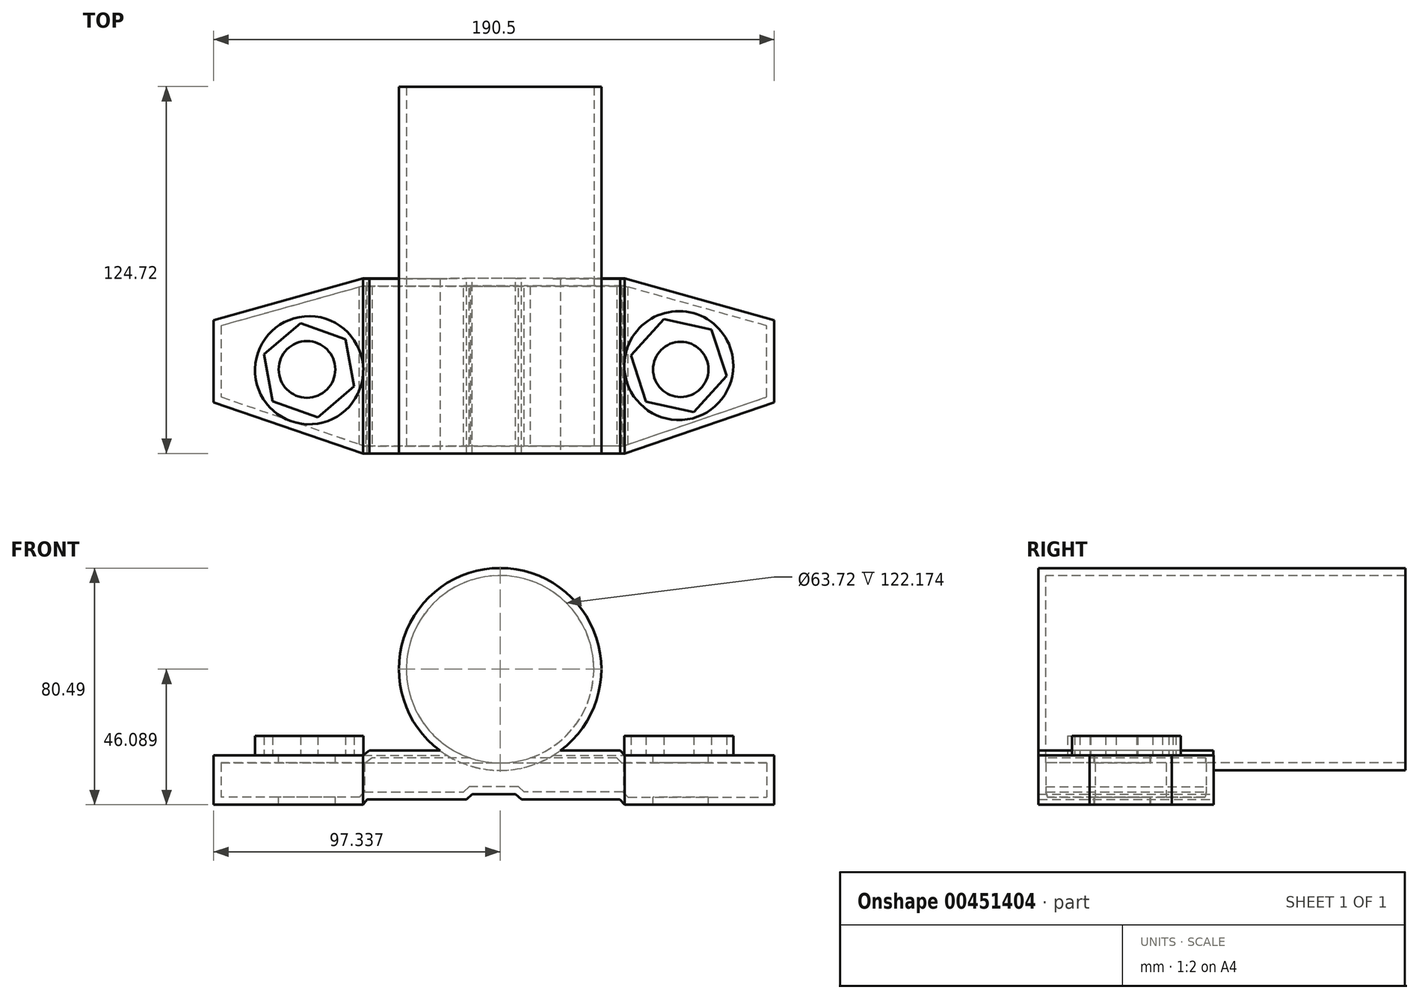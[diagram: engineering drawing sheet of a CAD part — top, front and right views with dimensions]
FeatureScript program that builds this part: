
annotation { "Feature Type Name" : "Feature", "Feature Type Description" : "" }
export const myFeature = defineFeature(function(context is Context, id is Id, definition is map)
    precondition{}
    {
        {
            var Q0;
            Q0=qCreatedBy(makeId("Top.planeOp"),FACE);
            var sketch = newSketch(context, id + "F0", { "sketchPlane" : qUnion([Q0])});
            skLineSegment(sketch, "E0", {"start": v(-14.1, 0) * mm, "end": v(74.8, 0) * mm});
            skLineSegment(sketch, "E1", {"start": v(-14.1, 0) * mm, "end": v(-64.9, -14.2) * mm});
            skLineSegment(sketch, "E2", {"start": v(-64.9, -14.2) * mm, "end": v(-64.9, -42.14) * mm});
            skLineSegment(sketch, "E3", {"start": v(-64.9, -42.14) * mm, "end": v(-14.1, -59.52) * mm});
            skLineSegment(sketch, "E4", {"start": v(-14.1, -59.52) * mm, "end": v(74.8, -59.52) * mm});
            skLineSegment(sketch, "E5", {"start": v(74.8, -59.52) * mm, "end": v(125.6, -42.14) * mm});
            skLineSegment(sketch, "E6", {"start": v(125.6, -42.14) * mm, "end": v(125.6, -14.2) * mm});
            skLineSegment(sketch, "E7", {"start": v(125.6, -14.2) * mm, "end": v(74.8, 0) * mm});
            skSolve(sketch);
        }
        {
            var Q0;
            Q0 = qSketchRegion(id + "F0", true);
            extrude(context, id + "F1", {"entities" : qUnion([Q0]), "depth" : 16.76 * mm});
        }
        {
            var Q0;
            Q0=makeQuery(id+"F1.opExtrude","SWEPT_FACE",FACE,{"disambiguationData":[OSD([sQuery(id+"F0.wireOp",EDGE,"E0")])]});
            var sketch = newSketch(context, id + "F2", { "sketchPlane" : qUnion([Q0])});
            skLineSegment(sketch, "E8", {"start": v(-74.8, 0) * mm, "end": v(-73.06, 1.86) * mm});
            skLineSegment(sketch, "E9", {"start": v(14.1, 0) * mm, "end": v(12.68, 1.86) * mm});
            skLineSegment(sketch, "E10", {"start": v(12.68, 1.86) * mm, "end": v(-25.13, 1.86) * mm});
            skLineSegment(sketch, "E11", {"start": v(-73.06, 1.86) * mm, "end": v(-35.26, 1.86) * mm});
            skLineSegment(sketch, "E12", {"start": v(-35.26, 1.86) * mm, "end": v(-33.63, 3.58) * mm});
            skLineSegment(sketch, "E13", {"start": v(-33.63, 3.58) * mm, "end": v(-26.63, 3.58) * mm});
            skLineSegment(sketch, "E14", {"start": v(-26.63, 3.58) * mm, "end": v(-25.13, 1.86) * mm});
            skLineSegment(sketch, "E15", {"start": v(14.1, 0) * mm, "end": v(-74.8, 0) * mm});
            skSolve(sketch);
        }
        {
            var Q0;
            Q0 = qSketchRegion(id + "F2", true);
            extrude(context, id + "F3", {"entities" : qUnion([Q0]), "operationType" : NewBodyOperationType.REMOVE, "oppositeDirection" : true, "depth" : 68.83 * mm});
        }
        {
            var Q0;
            Q0=makeQuery(id+"F1.opExtrude","SWEPT_FACE",FACE,{"disambiguationData":[OSD([sQuery(id+"F0.wireOp",EDGE,"E0")])]});
            var sketch = newSketch(context, id + "F4", { "sketchPlane" : qUnion([Q0])});
            skLineSegment(sketch, "E16", {"start": v(-26.63, 3.58) * mm, "end": v(-22.92, 3.58) * mm});
            skLineSegment(sketch, "E17", {"start": v(-22.92, 3.58) * mm, "end": v(-22.92, 1.86) * mm});
            skLineSegment(sketch, "E18", {"start": v(-22.92, 1.86) * mm, "end": v(-25.13, 1.86) * mm});
            skLineSegment(sketch, "E19", {"start": v(-25.13, 1.86) * mm, "end": v(-26.63, 3.58) * mm});
            skLineSegment(sketch, "E20", {"start": v(-33.63, 3.58) * mm, "end": v(-37.75, 3.58) * mm});
            skLineSegment(sketch, "E21", {"start": v(-37.75, 3.58) * mm, "end": v(-39.67, 1.86) * mm});
            skLineSegment(sketch, "E22", {"start": v(-39.67, 1.86) * mm, "end": v(-35.26, 1.86) * mm});
            skLineSegment(sketch, "E23", {"start": v(-35.26, 1.86) * mm, "end": v(-33.63, 3.58) * mm});
            skSolve(sketch);
        }
        {
            var Q0;
            Q0 = qSketchRegion(id + "F4", true);
            extrude(context, id + "F5", {"entities" : qUnion([Q0]), "operationType" : NewBodyOperationType.REMOVE, "oppositeDirection" : true, "depth" : 73.15 * mm});
        }
        {
            var Q0;
            Q0=makeQuery(id+"F1.opExtrude","SWEPT_FACE",FACE,{"disambiguationData":[OSD([sQuery(id+"F0.wireOp",EDGE,"E0")])]});
            var sketch = newSketch(context, id + "F6", { "sketchPlane" : qUnion([Q0])});
            skLineSegment(sketch, "E24", {"start": v(-22.92, 3.58) * mm, "end": v(-21.07, 1.86) * mm});
            skLineSegment(sketch, "E25", {"start": v(-21.07, 1.86) * mm, "end": v(-22.92, 1.86) * mm});
            skLineSegment(sketch, "E26", {"start": v(-22.92, 1.86) * mm, "end": v(-22.92, 3.58) * mm});
            skSolve(sketch);
        }
        {
            var Q0;
            Q0 = qSketchRegion(id + "F6", true);
            extrude(context, id + "F7", {"entities" : qUnion([Q0]), "operationType" : NewBodyOperationType.REMOVE, "oppositeDirection" : true, "depth" : 106.93 * mm});
        }
        {
            var Q0;
            Q0=makeQuery(id+"F1.opExtrude","SWEPT_FACE",FACE,{"disambiguationData":[OSD([sQuery(id+"F0.wireOp",EDGE,"E4")])]});
            var sketch = newSketch(context, id + "F8", { "sketchPlane" : qUnion([Q0])});
            skLineSegment(sketch, "E27", {"start": v(74.8, 16.76) * mm, "end": v(73.19, 18.44) * mm});
            skLineSegment(sketch, "E28", {"start": v(73.19, 18.44) * mm, "end": v(-11.98, 18.44) * mm});
            skLineSegment(sketch, "E29", {"start": v(-11.98, 18.44) * mm, "end": v(-14.1, 16.76) * mm});
            skLineSegment(sketch, "E30", {"start": v(-14.1, 16.76) * mm, "end": v(74.8, 16.76) * mm});
            skSolve(sketch);
        }
        {
            var Q0;
            Q0 = qSketchRegion(id + "F8", true);
            extrude(context, id + "F9", {"entities" : qUnion([Q0]), "operationType" : NewBodyOperationType.ADD, "oppositeDirection" : true, "depth" : 59.44 * mm});
        }
        {
            var Q0;
            Q0=makeQuery(id+"F9.boolean.opBoolean","MERGE",FACE,{"derivedFrom":[makeQuery(id+"F1.opExtrude","SWEPT_FACE",FACE,{"disambiguationData":[OSD([sQuery(id+"F0.wireOp",EDGE,"E4")])]}),makeQuery(id+"F9.opExtrude","CAP_FACE",FACE,{"disambiguationData":[OSD([sQuery(id+"F8.wireOp",EDGE,"E27"),sQuery(id+"F8.wireOp",EDGE,"E28"),sQuery(id+"F8.wireOp",EDGE,"E29"),sQuery(id+"F8.wireOp",EDGE,"E30")])],"isStart":true})]});
            var sketch = newSketch(context, id + "F10", { "sketchPlane" : qUnion([Q0])});
            skCircle(sketch, "E31", {"center": v(32.45, 46.09) * mm, "radius": 34.4 * mm});
            skSolve(sketch);
        }
        {
            var Q0;
            Q0 = qSketchRegion(id + "F10", true);
            extrude(context, id + "F11", {"entities" : qUnion([Q0]), "operationType" : NewBodyOperationType.ADD, "oppositeDirection" : true, "depth" : 124.7 * mm});
        }
        {
            var Q0;
            Q0=makeQuery(id+"F11.opExtrude","CAP_FACE",FACE,{"disambiguationData":[OSD([sQuery(id+"F10.wireOp",EDGE,"E31")])],"isStart":false});
            shell(context, id + "F12", {"entities" : qUnion([Q0]), "thickness" : 2.54 * mm});
        }
        {
            var Q0;
            {var subQ0=sQuery(id+"F0.wireOp",EDGE,"E6");var subQ1=sQuery(id+"F0.wireOp",EDGE,"E5");var subQ6=sQuery(id+"F0.wireOp",EDGE,"E4");var subQ7=sQuery(id+"F0.wireOp",EDGE,"E0");var subQ9=sQuery(id+"F0.wireOp",EDGE,"E7");Q0=makeQuery(id+"F11.boolean.opBoolean","SPLIT",FACE,{"disambiguationData":[TD([makeQuery(id+"F1.opExtrude","SWEPT_FACE",FACE,{"disambiguationData":[OSD([subQ1])]})])],"derivedFrom":makeQuery(id+"F1.opExtrude","CAP_FACE",FACE,{"disambiguationData":[OSD([subQ7,sQuery(id+"F0.wireOp",EDGE,"E1"),sQuery(id+"F0.wireOp",EDGE,"E2"),sQuery(id+"F0.wireOp",EDGE,"E3"),subQ6,subQ1,subQ0,subQ9])],"isStart":false})});}
            var sketch = newSketch(context, id + "F13", { "sketchPlane" : qUnion([Q0])});
            skCircle(sketch, "E32", {"center": v(93.18, -29.68) * mm, "radius": 18.5 * mm});
            skPoint(sketch, "E32.first.point", {"position": v(74.8, -31.91) * mm});
            skPoint(sketch, "E32.second.point", {"position": v(111.54, -27.4) * mm});
            skPoint(sketch, "E32.third.point", {"position": v(111.6, -31.35) * mm});
            skCircle(sketch, "E33", {"center": v(-32.44, -31.25) * mm, "radius": 18.38 * mm});
            skPoint(sketch, "E33.first.point", {"position": v(-14.06, -31.35) * mm});
            skPoint(sketch, "E33.second.point", {"position": v(-50.83, -31.35) * mm});
            skPoint(sketch, "E33.third.point", {"position": v(-50.55, -28.1) * mm});
            skCircle(sketch, "E34.cCircle", {"center": v(93.18, -29.68) * mm, "radius": 14.36 * mm, "construction": true});
            skLineSegment(sketch, "E34.0", {"start": v(98.28, -45.46) * mm, "end": v(82.06, -41.99) * mm});
            skLineSegment(sketch, "E34.1", {"start": v(82.06, -41.99) * mm, "end": v(76.96, -26.2) * mm});
            skLineSegment(sketch, "E34.2", {"start": v(76.96, -26.2) * mm, "end": v(88.07, -13.9) * mm});
            skLineSegment(sketch, "E34.3", {"start": v(88.07, -13.9) * mm, "end": v(104.3, -17.36) * mm});
            skLineSegment(sketch, "E34.4", {"start": v(104.3, -17.36) * mm, "end": v(109.4, -33.15) * mm});
            skLineSegment(sketch, "E34.5", {"start": v(109.4, -33.15) * mm, "end": v(98.28, -45.46) * mm});
            skPoint(sketch, "E34.0.midPoint", {"position": v(90.17, -43.72) * mm});
            skCircle(sketch, "E35.cCircle", {"center": v(-32.44, -31.25) * mm, "radius": 14.1 * mm, "construction": true});
            skLineSegment(sketch, "E35.0", {"start": v(-29.51, -47.26) * mm, "end": v(-44.84, -41.8) * mm});
            skLineSegment(sketch, "E35.1", {"start": v(-44.84, -41.8) * mm, "end": v(-47.78, -25.79) * mm});
            skLineSegment(sketch, "E35.2", {"start": v(-47.78, -25.79) * mm, "end": v(-35.38, -15.24) * mm});
            skLineSegment(sketch, "E35.3", {"start": v(-35.38, -15.24) * mm, "end": v(-20.05, -20.7) * mm});
            skLineSegment(sketch, "E35.4", {"start": v(-20.05, -20.7) * mm, "end": v(-17.11, -36.72) * mm});
            skLineSegment(sketch, "E35.5", {"start": v(-17.11, -36.72) * mm, "end": v(-29.51, -47.26) * mm});
            skPoint(sketch, "E35.0.midPoint", {"position": v(-37.18, -44.53) * mm});
            skSolve(sketch);
        }
        {
            var Q0;
            Q0 = qSketchRegion(id + "F13", true);
            extrude(context, id + "F14", {"entities" : qUnion([Q0]), "operationType" : NewBodyOperationType.ADD, "depth" : 6.6 * mm});
        }
        {
            var Q0;
            {var subQ0=sQuery(id+"F0.wireOp",EDGE,"E6");var subQ1=sQuery(id+"F0.wireOp",EDGE,"E5");var subQ6=sQuery(id+"F0.wireOp",EDGE,"E4");var subQ7=sQuery(id+"F0.wireOp",EDGE,"E0");var subQ9=sQuery(id+"F0.wireOp",EDGE,"E7");Q0=makeQuery(id+"F14.boolean.opBoolean","SPLIT",FACE,{"disambiguationData":[TD([makeQuery(id+"F14.opExtrude","SWEPT_FACE",FACE,{"disambiguationData":[OSD([sQuery(id+"F13.wireOp",EDGE,"E34.0")])]})])],"derivedFrom":makeQuery(id+"F11.boolean.opBoolean","SPLIT",FACE,{"disambiguationData":[TD([makeQuery(id+"F1.opExtrude","SWEPT_FACE",FACE,{"disambiguationData":[OSD([subQ1])]})])],"derivedFrom":makeQuery(id+"F1.opExtrude","CAP_FACE",FACE,{"disambiguationData":[OSD([subQ7,sQuery(id+"F0.wireOp",EDGE,"E1"),sQuery(id+"F0.wireOp",EDGE,"E2"),sQuery(id+"F0.wireOp",EDGE,"E3"),subQ6,subQ1,subQ0,subQ9])],"isStart":false})})});}
            var sketch = newSketch(context, id + "F15", { "sketchPlane" : qUnion([Q0])});
            skCircle(sketch, "E36", {"center": v(-33.18, -30.97) * mm, "radius": 9.62 * mm});
            skCircle(sketch, "E37", {"center": v(93.84, -30.97) * mm, "radius": 9.4 * mm});
            skSolve(sketch);
        }
        {
            var Q0;
            Q0 = qSketchRegion(id + "F15", true);
            extrude(context, id + "F16", {"entities" : qUnion([Q0]), "operationType" : NewBodyOperationType.REMOVE, "oppositeDirection" : true, "depth" : 107.19 * mm});
        }
    });
